# Revit family: SRT1-Surface
name_source: partatom
category: Lighting Fixtures
revit_build: Autodesk Revit 2014 (Build: 20130308_1515(x64)
units: mm (PartAtom-declared; Revit-internal decimal feet)

## types (1)
- SRT1
    Apparent Load = 25 VA
    Ballast = Paint - Hubbell - Carbon Black
    Certifications = • cCSAus certified to UL 1598
• Wall Mount: Suitable for wet locations
• Surface & Pendant Mount: Suitable for wet
locations under covered ceiling
• Cord Mount and all Wall Wash: Suitable for
damp locations
    Color Filter = 16777215
    Cord Height = 17.5 "
    Default Elevation = 48 "
    Description = Small Edge-Lit luminaire, the ideal solution for parking garage and canopy applications. Provides exceptional visual comfort and photometric performance in sleek low profile housing. Available in a wide range of lumen outputs and photometric distributions paired with a specially designed lens for optimal visual comfort and performance.
    Dimming Lamp Color Temperature Shift = <None>
    Emit Shape Visible in Rendering = No
    Emit from Circle Diameter = 4 "
    Features = •	Compact and low profile housing measuring 12inch x 3.1inch
•	Visual comfort edge-lit design
•	2,500-6,000 lumens
•	Option uplight module provides 800 lumens of indirect illumination
•	Surface and pendant mounting options
•	Control options including occupancy sensing with photocontrol
•	Optional bird shield and vandal deterring wire guard
    Lamp = LED Lamp
    Manufacturer = Beacon
    Model = SRT1
    Photometric Web File = SRT1-55-3K7-5C.ies
    Product Documentation Link = https://hubbellcdn.com
    Product Page URL = https://www.hubbell.com
    Reflector = Glass - Hubbell - Glass
    Tilt Angle = -90.00°
    URL = https://www.hubbell.com
    Voltage = 120 V
    Warranty = • 5 year warranty
• See HLI Standard Warranty for
additional information
    Wattage Comments = 20-55W

## geometry (parser evidence)
native form markers: Blend x12, Sweep x2
no freeform markers — native parametric forms only
